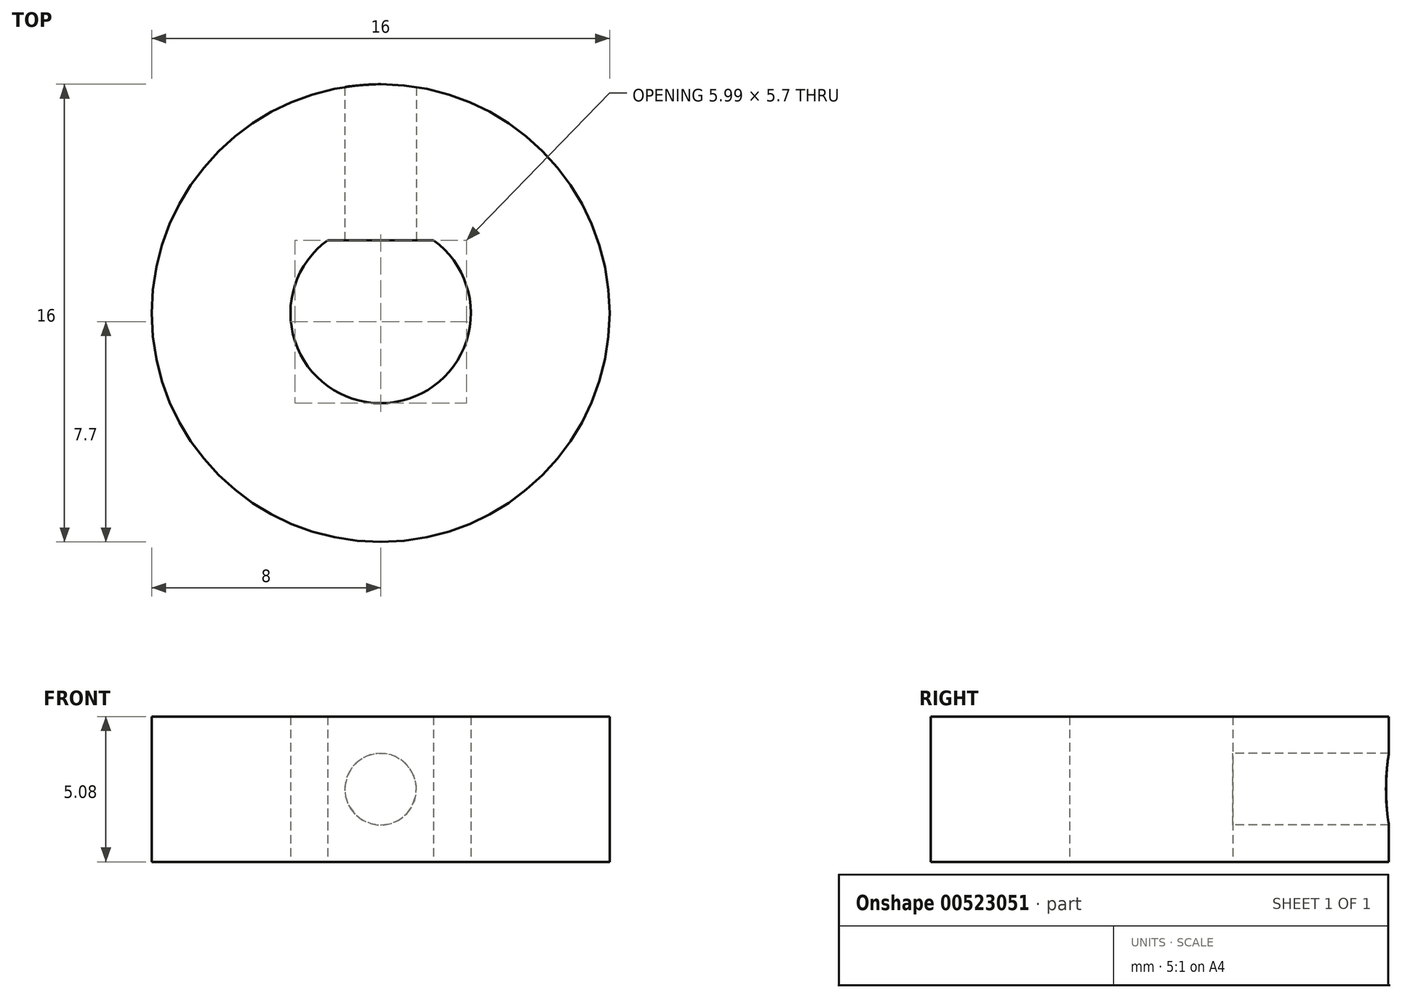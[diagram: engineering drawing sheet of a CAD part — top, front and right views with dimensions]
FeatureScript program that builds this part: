
annotation { "Feature Type Name" : "Feature", "Feature Type Description" : "" }
export const myFeature = defineFeature(function(context is Context, id is Id, definition is map)
    precondition{}
    {
        {
            var Q0;
            Q0=qCreatedBy(makeId("Top.planeOp"),FACE);
            var sketch = newSketch(context, id + "F0", { "sketchPlane" : qUnion([Q0])});
            skCircle(sketch, "E0", {"center": v(0, 0) * mm, "radius": 3.15 * mm});
            skCircle(sketch, "E1", {"center": v(0, 0) * mm, "radius": 8 * mm});
            skLineSegment(sketch, "E2", {"start": v(0, 0) * mm, "end": v(0, 2.55) * mm});
            skLineSegment(sketch, "E3", {"start": v(0, 2.55) * mm, "end": v(-1.85, 2.55) * mm});
            skLineSegment(sketch, "E4", {"start": v(0, 2.55) * mm, "end": v(1.85, 2.55) * mm});
            skSolve(sketch);
        }
        {
            var Q0;
            Q0=makeQuery(id+"F0.imprint","IMPRINT",FACE,{"disambiguationData":[TD([[makeQuery(id+"F0.imprint","IMPRINT",EDGE,{"derivedFrom":sQuery(id+"F0.wireOp",EDGE,"E1")}),1.0]])]});
            var Q1;
            {var subQ0=sQuery(id+"F0.wireOp",EDGE,"E3");Q1=makeQuery(id+"F0.imprint","IMPRINT",FACE,{"disambiguationData":[TD([[makeQuery(id+"F0.imprint","IMPRINT",EDGE,{"derivedFrom":subQ0}),-1.0]])]});}
            extrude(context, id + "F1", {"entities" : qUnion([Q0, Q1]), "depth" : 5.08 * mm, "offsetDistance" : 25.4 * mm});
        }
        {
            var Q0;
            Q0=makeQuery(id+"F1.opExtrude","SWEPT_FACE",FACE,{"disambiguationData":[OSD([sQuery(id+"F0.wireOp",EDGE,"E3"),sQuery(id+"F0.wireOp",EDGE,"E4")])]});
            var sketch = newSketch(context, id + "F2", { "sketchPlane" : qUnion([Q0])});
            skCircle(sketch, "E5", {"center": v(0, 2.54) * mm, "radius": 1.25 * mm});
            skSolve(sketch);
        }
        {
            var Q0;
            Q0=makeQuery(id+"F2.imprint","IMPRINT",FACE,{"disambiguationData":[TD([[makeQuery(id+"F2.imprint","IMPRINT",EDGE,{"derivedFrom":sQuery(id+"F2.wireOp",EDGE,"E5")}),1.0]])]});
            extrude(context, id + "F3", {"entities" : qUnion([Q0]), "operationType" : NewBodyOperationType.REMOVE, "oppositeDirection" : true, "depth" : 25.4 * mm, "offsetDistance" : 25.4 * mm});
        }
    });
